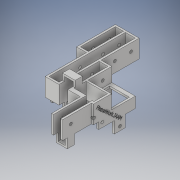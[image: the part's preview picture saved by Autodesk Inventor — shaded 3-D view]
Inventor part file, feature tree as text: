
AUTODESK INVENTOR PART (.ipt)
format: ipt  version: 2017 (Build 210142000, 142)  size: 843,776 bytes
history: native  units: mm
features: sketch x22, extrude x11, hole x6, plane x2, sweep x2, emboss x1, other x1
ambient origin geometry x8: Origin, YZ Plane, XZ Plane, XY Plane, X Axis, Y Axis, Z Axis, Center Point
bodies: Solid1 (feature_tree)
feature tree (45):
  extrude  "Extrusion1"  Depth=25.0mm TaperAngle=0.0deg
  extrude  "Extrusion2"  Depth=32.0mm
  plane  "Work Plane1"
  sketch  "Sketch4"  dims[d20=2.033mm d21=32.0mm]
  sweep  "Sweep1"
  sketch  "Sketch7"  dims[d24=0.8mm d25=0.8mm]
  plane  "Work Plane2"
  sweep  "Sweep2"
  hole  "Hole1"  [1 undecoded]
  hole  "Hole2"  [1 undecoded]
  hole  "Hole3"  [1 undecoded]
  extrude  "Extrusion3"  Depth=3.0mm
  hole  "Hole6"  [1 undecoded]
  hole  "Hole7"  [1 undecoded]
  sketch  "Sketch17"  dims[d65=2.2mm d66=25.5mm d67=26.6mm]
  extrude  "Extrusion4"  Depth=0.8mm
  extrude  "Extrusion5"  Depth=0.8mm
  extrude  "Extrusion6"  Depth=18.0mm
  hole  "Hole8"  [1 undecoded]
  extrude  "Extrusion7"  Depth=45.0mm
  extrude  "Extrusion8"  Depth=0.8mm
  extrude  "Extrusion9"  Depth=8.0mm
  extrude  "Extrusion10"  Depth=2.2mm
  emboss  "Emboss1"
  sketch  "Sketch1"  dims[d0=84.000163mm d1=25.0mm d2=6.0mm d3=44.0mm d4=30.0mm d5=29.5mm d6=22.0mm d7=16.5mm d8=64.5mm d9=76.0mm d10=0.0mm d12=30.0mm d13=0.0mm]
  other  "Srf1"
  sketch  "Sketch2"  dims[d14=0.8mm d15=32.0mm d17=2.033mm]
  sketch  "Sketch3"  dims[d18=14.0mm d19=32.0mm]
  sketch  "Sketch6"  dims[d22=84.000163mm d23=0.8mm]
  sketch  "Sketch8"  dims[d26=0.8mm d28=0.8mm]
  sketch  "Sketch9"  dims[d33=3.0mm d35=3.0mm]
  sketch  "Sketch10"  dims[d36=3.0mm d37=5.6mm]
  sketch  "Sketch11"  dims[d38=3.0mm d43=0.8mm]
  sketch  "Sketch12"  dims[d44=0.8mm d45=9.0mm]
  sketch  "Sketch15"  dims[d53=10.0mm d57=0.8mm]
  sketch  "Sketch16"  dims[d59=3.0mm d60=2.2mm d63=18.0mm]
  sketch  "Sketch18"  dims[d68=30.5mm d69=45.0mm]
  sketch  "Sketch19"  dims[d70=2.2mm d71=0.8mm]
  sketch  "Sketch20"  dims[d72=2.2mm d74=8.0mm]
  sketch  "Sketch21"  dims[d75=8.0mm d76=2.2mm]
  sketch  "Sketch23"  dims[d77=2.2mm d78=0.8mm d79=21.3mm d80=20.971377mm]
  sketch  "Sketch24"  dims[d81=2.2mm]
  sketch  "Sketch25"  dims[d82=2.2mm]
  sketch  "Sketch26"  dims[d83=14.0mm d84=18.0mm d85=2.2mm d86=0.8mm d87=29.550081mm d88=2.2mm d89=4.8mm d90=2.2mm d91=2.2mm d92=2.2mm d93=2.2mm d94=2.2mm d95=40.3mm d96=85.0mm d97=42.5mm d98=11.049919mm d99=2.2mm d100=20.0mm d101=0.0mm d102=2.2mm d103=2.2mm d104=2.2mm d105=2.2mm d106=20.0mm d107=0.0mm d108=34.6mm d109=4.9145mm d110=2.24mm d111=27.0mm d112=9.69291mm d113=4.95473mm d114=1.1mm d115=1.1mm d116=28.1mm d117=2.2mm d118=0.0mm d119=8.0mm d120=6.0mm d121=0.0mm d122=0.0mm d123=9.0mm d124=8.5mm d125=-9.0mm d126=4.0mm d127=8.5mm d128=1.1mm d129=1.1mm d130=21.0mm d131=0.0mm d132=0.0mm d134=8.0mm d135=5.0mm d136=0.0mm d137=0.0mm d138=9.2mm d139=8.5mm d140=18.0mm d141=8.5mm d143=25.5mm d144=8.5mm d145=3.302mm d146=8.331mm d147=4.0mm d148=2.0mm d149=90.0deg d150=12.3mm d151=20.594885mm d152=8.5mm d153=52.7mm d154=3.302mm d155=8.331mm d156=4.0mm d157=2.0mm d158=90.0deg d159=12.3mm d160=20.594885mm d161=3.302mm d162=8.331mm d163=4.0mm d164=2.0mm d165=90.0deg d166=12.3mm d167=20.594885mm d168=8.0mm d169=2.2mm d170=0.0mm d171=6.0mm d172=8.0mm d173=2.2mm d174=8.0mm d175=2.2mm d176=8.0mm d177=2.2mm d178=0.0mm d179=0.0mm d180=0.0mm d181=7.5mm d182=0.0mm d203=30.0mm d204=26.656937mm d205=3.302mm d206=8.331mm d207=4.0mm d208=2.0mm d209=90.0deg d210=16.533mm d211=20.594885mm d212=12.5mm d214=3.302mm d215=8.331mm d216=4.0mm d217=2.0mm d218=90.0deg d219=16.533mm d220=20.594885mm d221=13.215633mm d222=24.0mm d223=32.78987mm d224=0.0mm d225=2.2mm d226=7.5mm d227=0.0mm d228=12.0mm d229=11.5mm d230=12.0mm d231=2.2mm d232=0.0mm d233=13.0mm d234=0.0mm d235=3.302mm d236=8.331mm d237=4.0mm d238=2.0mm d239=90.0deg d240=16.533mm d241=20.594885mm d242=29.0mm d243=0.0mm d245=2.2mm d246=4.416667mm d247=0.0mm d248=2.2mm d249=2.2mm d250=0.0mm d251=2.2mm d252=2.2mm d253=2.2mm d254=0.0mm d255=1.0mm d256=0.0mm d257=24.5mm]
  extrude  "ExtrusionSrf1"  Depth=0.8mm
note: 6 required parameter values undecoded (feature->parameter linkage not recoverable at this tier; creation-order binding heuristic only, values carry confidence <= 0.55)
